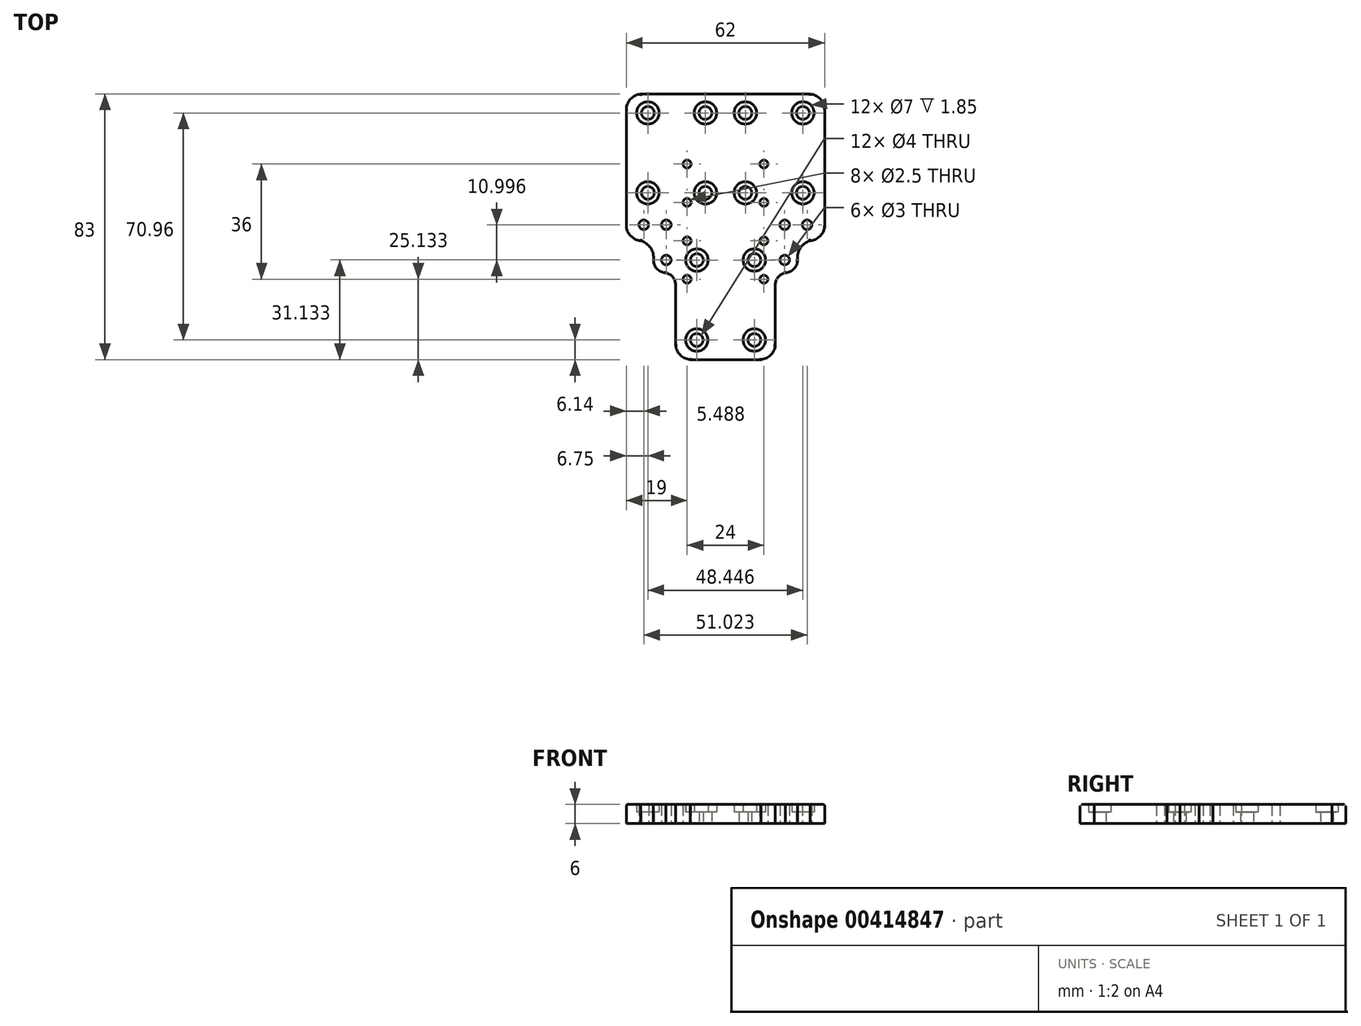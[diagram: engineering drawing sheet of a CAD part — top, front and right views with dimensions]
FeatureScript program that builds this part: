
annotation { "Feature Type Name" : "Feature", "Feature Type Description" : "" }
export const myFeature = defineFeature(function(context is Context, id is Id, definition is map)
    precondition{}
    {
        {
            var Q0;
            Q0=qCreatedBy(makeId("Top.planeOp"),FACE);
            cPlane(context, id + "F0", {"entities" : qUnion([Q0]), "cplaneType" : CPlaneType.OFFSET, "offset" : 15 * mm, "oppositeDirection" : true, "width" : 150 * mm, "height" : 150 * mm});
        }
        {
            var Q0;
            Q0=qCreatedBy(id+"F0.planeOp",FACE);
            var sketch = newSketch(context, id + "F1", { "sketchPlane" : qUnion([Q0])});
            skPoint(sketch, "E0.middle", {"position": v(0, 0) * mm});
            skLineSegment(sketch, "E1", {"start": v(-26.25, 37.6) * mm, "end": v(-22.25, 33.6) * mm, "construction": true});
            skLineSegment(sketch, "E2", {"start": v(-22.25, 37.6) * mm, "end": v(-26.25, 33.6) * mm, "construction": true});
            skLineSegment(sketch, "E3", {"start": v(-8.27, 37.6) * mm, "end": v(-4.27, 33.6) * mm, "construction": true});
            skLineSegment(sketch, "E4", {"start": v(-4.27, 37.6) * mm, "end": v(-8.27, 33.6) * mm, "construction": true});
            skLineSegment(sketch, "E5", {"start": v(4.21, 37.6) * mm, "end": v(8.21, 33.6) * mm, "construction": true});
            skLineSegment(sketch, "E6", {"start": v(8.21, 37.6) * mm, "end": v(4.21, 33.6) * mm, "construction": true});
            skLineSegment(sketch, "E7", {"start": v(22.2, 37.6) * mm, "end": v(26.2, 33.6) * mm, "construction": true});
            skLineSegment(sketch, "E8", {"start": v(26.2, 37.6) * mm, "end": v(22.2, 33.6) * mm, "construction": true});
            skLineSegment(sketch, "E9", {"start": v(-26.25, 12.63) * mm, "end": v(-22.25, 8.63) * mm, "construction": true});
            skLineSegment(sketch, "E10", {"start": v(-22.25, 12.63) * mm, "end": v(-26.25, 8.63) * mm, "construction": true});
            skLineSegment(sketch, "E11", {"start": v(-8.27, 12.63) * mm, "end": v(-4.27, 8.63) * mm, "construction": true});
            skLineSegment(sketch, "E12", {"start": v(-4.32, 12.68) * mm, "end": v(-8.32, 8.68) * mm, "construction": true});
            skLineSegment(sketch, "E13", {"start": v(4.21, 12.63) * mm, "end": v(8.21, 8.63) * mm, "construction": true});
            skLineSegment(sketch, "E14", {"start": v(8.22, 12.63) * mm, "end": v(4.21, 8.63) * mm, "construction": true});
            skLineSegment(sketch, "E15", {"start": v(22.2, 12.63) * mm, "end": v(26.2, 8.63) * mm, "construction": true});
            skLineSegment(sketch, "E16", {"start": v(26.2, 12.63) * mm, "end": v(22.2, 8.63) * mm, "construction": true});
            skLineSegment(sketch, "E17", {"start": v(-10.97, -8.37) * mm, "end": v(-6.88, -12.39) * mm, "construction": true});
            skLineSegment(sketch, "E18", {"start": v(-6.97, -8.37) * mm, "end": v(-10.97, -12.37) * mm, "construction": true});
            skLineSegment(sketch, "E19", {"start": v(7.01, -8.37) * mm, "end": v(11.01, -12.37) * mm, "construction": true});
            skLineSegment(sketch, "E20", {"start": v(11.01, -8.37) * mm, "end": v(7.01, -12.37) * mm, "construction": true});
            skLineSegment(sketch, "E21", {"start": v(-10.97, -33.36) * mm, "end": v(-6.97, -37.36) * mm, "construction": true});
            skLineSegment(sketch, "E22", {"start": v(-10.97, -37.36) * mm, "end": v(-6.97, -33.36) * mm, "construction": true});
            skLineSegment(sketch, "E23", {"start": v(7.01, -33.36) * mm, "end": v(11.01, -37.36) * mm, "construction": true});
            skLineSegment(sketch, "E24", {"start": v(7.01, -37.36) * mm, "end": v(11.01, -33.36) * mm, "construction": true});
            skCircle(sketch, "E25", {"center": v(-24.25, 35.6) * mm, "radius": 2 * mm});
            skCircle(sketch, "E26", {"center": v(-6.27, 35.6) * mm, "radius": 2 * mm});
            skCircle(sketch, "E27", {"center": v(6.21, 35.6) * mm, "radius": 2 * mm});
            skCircle(sketch, "E28", {"center": v(24.2, 35.6) * mm, "radius": 2 * mm});
            skCircle(sketch, "E29", {"center": v(24.2, 10.63) * mm, "radius": 2 * mm});
            skCircle(sketch, "E30", {"center": v(6.22, 10.63) * mm, "radius": 2 * mm});
            skCircle(sketch, "E31", {"center": v(-6.27, 10.63) * mm, "radius": 2 * mm});
            skCircle(sketch, "E32", {"center": v(-24.25, 10.63) * mm, "radius": 2 * mm});
            skCircle(sketch, "E33", {"center": v(-8.93, -10.38) * mm, "radius": 2 * mm});
            skCircle(sketch, "E34", {"center": v(9.01, -10.37) * mm, "radius": 2 * mm});
            skCircle(sketch, "E35", {"center": v(-8.97, -35.36) * mm, "radius": 2 * mm});
            skCircle(sketch, "E36", {"center": v(9.01, -35.36) * mm, "radius": 2 * mm});
            skCircle(sketch, "E37", {"center": v(-24.25, 35.6) * mm, "radius": 3.5 * mm});
            skCircle(sketch, "E38", {"center": v(-6.27, 35.6) * mm, "radius": 3.5 * mm});
            skCircle(sketch, "E39", {"center": v(6.21, 35.6) * mm, "radius": 3.5 * mm});
            skCircle(sketch, "E40", {"center": v(24.2, 35.6) * mm, "radius": 3.5 * mm});
            skCircle(sketch, "E41", {"center": v(-24.25, 10.63) * mm, "radius": 3.5 * mm});
            skCircle(sketch, "E42", {"center": v(-6.27, 10.63) * mm, "radius": 3.5 * mm});
            skCircle(sketch, "E43", {"center": v(6.22, 10.63) * mm, "radius": 3.5 * mm});
            skCircle(sketch, "E44", {"center": v(24.2, 10.63) * mm, "radius": 3.5 * mm});
            skCircle(sketch, "E45", {"center": v(-8.93, -10.38) * mm, "radius": 3.5 * mm});
            skCircle(sketch, "E46", {"center": v(9.01, -10.37) * mm, "radius": 3.5 * mm});
            skCircle(sketch, "E47", {"center": v(-8.97, -35.36) * mm, "radius": 3.5 * mm});
            skCircle(sketch, "E48", {"center": v(9.01, -35.36) * mm, "radius": 3.5 * mm});
            skLineSegment(sketch, "E49", {"start": v(0, 47.58) * mm, "end": v(0, -48.72) * mm, "construction": true});
            skLineSegment(sketch, "E50", {"start": v(-27.01, 2.13) * mm, "end": v(-24.01, -0.87) * mm});
            skLineSegment(sketch, "E51", {"start": v(-24.01, 2.13) * mm, "end": v(-27.01, -0.87) * mm, "construction": true});
            skLineSegment(sketch, "E52", {"start": v(-20, 2.13) * mm, "end": v(-17, -0.87) * mm, "construction": true});
            skLineSegment(sketch, "E53", {"start": v(-17, 2.13) * mm, "end": v(-20, -0.87) * mm, "construction": true});
            skLineSegment(sketch, "E54", {"start": v(17, 2.13) * mm, "end": v(20, -0.87) * mm, "construction": true});
            skLineSegment(sketch, "E55", {"start": v(20, 2.13) * mm, "end": v(17, -0.87) * mm, "construction": true});
            skLineSegment(sketch, "E56", {"start": v(24.01, 2.13) * mm, "end": v(27.01, -0.87) * mm, "construction": true});
            skLineSegment(sketch, "E57", {"start": v(27.01, 2.13) * mm, "end": v(24.01, -0.87) * mm, "construction": true});
            skLineSegment(sketch, "E58", {"start": v(17, -8.87) * mm, "end": v(20, -11.87) * mm, "construction": true});
            skLineSegment(sketch, "E59", {"start": v(20, -8.87) * mm, "end": v(17, -11.87) * mm, "construction": true});
            skLineSegment(sketch, "E60", {"start": v(-20, -8.87) * mm, "end": v(-17, -11.87) * mm, "construction": true});
            skLineSegment(sketch, "E61", {"start": v(-20, -11.87) * mm, "end": v(-17, -8.87) * mm, "construction": true});
            skCircle(sketch, "E62", {"center": v(25.51, 0.63) * mm, "radius": 1.5 * mm});
            skCircle(sketch, "E63", {"center": v(18.5, 0.63) * mm, "radius": 1.5 * mm});
            skCircle(sketch, "E64", {"center": v(18.5, -10.37) * mm, "radius": 1.5 * mm});
            skCircle(sketch, "E65", {"center": v(-18.5, 0.63) * mm, "radius": 1.5 * mm});
            skCircle(sketch, "E66", {"center": v(-25.51, 0.63) * mm, "radius": 1.5 * mm});
            skCircle(sketch, "E67", {"center": v(-18.5, -10.37) * mm, "radius": 1.5 * mm});
            skArc(sketch, "E68", {"start": v(-26.44, 41.5) * mm, "mid": v(-29.48, 40.1) * mm, "end": v(-31, 37.14) * mm});
            skArc(sketch, "E69.MirrorCS", {"start": v(26.44, 41.5) * mm, "mid": v(29.48, 40.1) * mm, "end": v(31, 37.14) * mm});
            skLineSegment(sketch, "E70", {"start": v(-34.26, 0) * mm, "end": v(34.55, 0) * mm, "construction": true});
            skLineSegment(sketch, "E71", {"start": v(26.44, 41.5) * mm, "end": v(-26.44, 41.5) * mm});
            skLineSegment(sketch, "E72.left", {"start": v(12, -16.37) * mm, "end": v(12, -4.37) * mm, "construction": true});
            skLineSegment(sketch, "E72.right", {"start": v(-12, -16.37) * mm, "end": v(-12, -4.37) * mm, "construction": true});
            skCircle(sketch, "E73", {"center": v(0, 0) * mm, "radius": 1 * mm, "construction": true});
            skLineSegment(sketch, "E74", {"start": v(-12, -16.37) * mm, "end": v(12, -16.37) * mm, "construction": true});
            skLineSegment(sketch, "E75", {"start": v(-12, -4.37) * mm, "end": v(12, -4.37) * mm, "construction": true});
            skCircle(sketch, "E76", {"center": v(12, -4.37) * mm, "radius": 1.25 * mm});
            skCircle(sketch, "E77.MirrorC", {"center": v(-12, -4.37) * mm, "radius": 1.25 * mm});
            skCircle(sketch, "E78.MirrorC", {"center": v(12, -16.37) * mm, "radius": 1.25 * mm});
            skCircle(sketch, "E79.MirrorC", {"center": v(-12, -16.37) * mm, "radius": 1.25 * mm});
            skLineSegment(sketch, "E80.left", {"start": v(12, -4.37) * mm, "end": v(12, 7.63) * mm, "construction": true});
            skLineSegment(sketch, "E80.right", {"start": v(-12, -4.37) * mm, "end": v(-12, 7.63) * mm, "construction": true});
            skLineSegment(sketch, "E81", {"start": v(-12, 7.63) * mm, "end": v(12, 7.63) * mm, "construction": true});
            skCircle(sketch, "E82", {"center": v(12, 7.63) * mm, "radius": 1.25 * mm});
            skCircle(sketch, "E83.MirrorC", {"center": v(-12, 7.63) * mm, "radius": 1.25 * mm});
            skLineSegment(sketch, "E84.left", {"start": v(12, 7.63) * mm, "end": v(12, 19.63) * mm, "construction": true});
            skLineSegment(sketch, "E84.right", {"start": v(-12, 7.63) * mm, "end": v(-12, 19.63) * mm, "construction": true});
            skLineSegment(sketch, "E85", {"start": v(-12, 19.63) * mm, "end": v(12, 19.63) * mm, "construction": true});
            skCircle(sketch, "E86", {"center": v(12, 19.63) * mm, "radius": 1.25 * mm});
            skCircle(sketch, "E87.MirrorC", {"center": v(-12, 19.63) * mm, "radius": 1.25 * mm});
            skArc(sketch, "E88.MirrorCS", {"start": v(26.44, -4.36) * mm, "mid": v(29.48, -2.97) * mm, "end": v(31, 0) * mm});
            skLineSegment(sketch, "E89", {"start": v(31, 37.14) * mm, "end": v(31, 0) * mm});
            skArc(sketch, "E90.MirrorCS", {"start": v(-26.44, -4.36) * mm, "mid": v(-29.48, -2.97) * mm, "end": v(-31, 0) * mm});
            skLineSegment(sketch, "E91", {"start": v(-31, 37.14) * mm, "end": v(-31, 0) * mm});
            skArc(sketch, "E92.MirrorCS", {"start": v(-11.03, -41.5) * mm, "mid": v(-14.07, -40.1) * mm, "end": v(-15.59, -37.14) * mm});
            skArc(sketch, "E93", {"start": v(-22.51, -10.35) * mm, "mid": v(-23.37, -6.63) * mm, "end": v(-26.44, -4.36) * mm});
            skLineSegment(sketch, "E94", {"start": v(-15.59, -37.14) * mm, "end": v(-15.59, -18.13) * mm});
            skArc(sketch, "E95", {"start": v(-15.59, -18.13) * mm, "mid": v(-16.45, -15.7) * mm, "end": v(-18.66, -14.37) * mm});
            skArc(sketch, "E96", {"start": v(-22.51, -10.35) * mm, "mid": v(-21.4, -13.14) * mm, "end": v(-18.66, -14.37) * mm});
            skArc(sketch, "E97.MirrorCS", {"start": v(22.51, -10.35) * mm, "mid": v(23.37, -6.63) * mm, "end": v(26.44, -4.36) * mm});
            skArc(sketch, "E98.MirrorCS", {"start": v(22.51, -10.35) * mm, "mid": v(21.4, -13.14) * mm, "end": v(18.66, -14.37) * mm});
            skArc(sketch, "E99.MirrorCS", {"start": v(15.59, -18.13) * mm, "mid": v(16.45, -15.7) * mm, "end": v(18.66, -14.37) * mm});
            skLineSegment(sketch, "E100.MirrorCS", {"start": v(15.59, -37.14) * mm, "end": v(15.59, -18.13) * mm});
            skArc(sketch, "E101.MirrorCS", {"start": v(11.03, -41.5) * mm, "mid": v(14.07, -40.1) * mm, "end": v(15.59, -37.14) * mm});
            skLineSegment(sketch, "E102", {"start": v(-11.03, -41.5) * mm, "end": v(11.03, -41.5) * mm});
            skSolve(sketch);
        }
        {
            var Q0;
            Q0=makeQuery(id+"F1.imprint","IMPRINT",FACE,{"disambiguationData":[TD([[makeQuery(id+"F1.imprint","IMPRINT",EDGE,{"derivedFrom":sQuery(id+"F1.wireOp",EDGE,"E37")}),-1.0]])]});
            var Q1;
            {var subQ12=sQuery(id+"F1.wireOp",EDGE,"pzuTnQxO-lV87-fYSm-Gx9G-mAiwIQIc8dDl");Q1=makeQuery(id+"F1.imprint","IMPRINT",FACE,{"disambiguationData":[TD([[makeQuery(id+"F1.imprint","IMPRINT",EDGE,{"derivedFrom":subQ12}),-1.0]])]});}
            var Q2;
            {var subQ1=sQuery(id+"F1.wireOp",EDGE,"pzuTnQxO-lV87-fYSm-Gx9G-mAiwIQIc8dDl");Q2=makeQuery(id+"F1.imprint","IMPRINT",FACE,{"disambiguationData":[TD([[makeQuery(id+"F1.imprint","IMPRINT",EDGE,{"derivedFrom":subQ1}),1.0]])]});}
            var Q3;
            {var subQ12=sQuery(id+"F1.wireOp",EDGE,"efa04ed1-a487-4949-b661-946b3568b5050.MirrorCS");Q3=makeQuery(id+"F1.imprint","IMPRINT",FACE,{"disambiguationData":[TD([[makeQuery(id+"F1.imprint","IMPRINT",EDGE,{"derivedFrom":subQ12}),1.0]])]});}
            var Q4;
            {var subQ4=sQuery(id+"F1.wireOp",EDGE,"E72.left");Q4=makeQuery(id+"F1.imprint","IMPRINT",FACE,{"disambiguationData":[TD([[makeQuery(id+"F1.imprint","IMPRINT",EDGE,{"derivedFrom":subQ4}),1.0]])]});}
            var Q5;
            {var subQ1=sQuery(id+"F1.wireOp",EDGE,"jk487AJZ-i1Am-lmEW-zcT6-8KVyPQAgBlb1.bottom");Q5=makeQuery(id+"F1.imprint","IMPRINT",FACE,{"disambiguationData":[TD([[makeQuery(id+"F1.imprint","IMPRINT",EDGE,{"derivedFrom":subQ1}),-1.0]])]});}
            var Q6;
            {var subQ4=sQuery(id+"F1.wireOp",EDGE,"E72.right");Q6=makeQuery(id+"F1.imprint","IMPRINT",FACE,{"disambiguationData":[TD([[makeQuery(id+"F1.imprint","IMPRINT",EDGE,{"derivedFrom":subQ4}),-1.0]])]});}
            var Q7;
            {var subQ1=sQuery(id+"F1.wireOp",EDGE,"jk487AJZ-i1Am-lmEW-zcT6-8KVyPQAgBlb1.left");var subQ3=sQuery(id+"F1.wireOp",EDGE,"8fUSbGhS-PyZG-xoJf-GsF2-3zE0cOOII221");var subQ4=makeQuery(id+"F1.imprint","INTERSECT",VERTEX,{"derivedFrom":[subQ1,subQ3]});Q7=makeQuery(id+"F1.imprint","IMPRINT",FACE,{"disambiguationData":[TD([[makeQuery(id+"F1.imprint","IMPRINT",EDGE,{"disambiguationData":[TD([[subQ4,-1.0]])],"derivedFrom":subQ3}),-1.0]])]});}
            var Q8;
            {var subQ0=sQuery(id+"F1.wireOp",EDGE,"FejcTz6K-61PN-e2Y3-l5dI-ztipBC45bLu5.bottom");var subQ1=sQuery(id+"F1.wireOp",EDGE,"jk487AJZ-i1Am-lmEW-zcT6-8KVyPQAgBlb1.right");var subQ2=makeQuery(id+"F1.imprint","INTERSECT",VERTEX,{"derivedFrom":[subQ1,subQ0]});Q8=makeQuery(id+"F1.imprint","IMPRINT",FACE,{"disambiguationData":[TD([[makeQuery(id+"F1.imprint","IMPRINT",EDGE,{"disambiguationData":[TD([[subQ2,1.0]])],"derivedFrom":subQ1}),-1.0]])]});}
            var Q9;
            {var subQ0=sQuery(id+"F1.wireOp",EDGE,"e855c95f-44d0-4618-945e-e5d8c2a51f020.MirrorCS");var subQ3=sQuery(id+"F1.wireOp",EDGE,"FejcTz6K-61PN-e2Y3-l5dI-ztipBC45bLu5.right");var subQ5=makeQuery(id+"F1.imprint","INTERSECT",VERTEX,{"derivedFrom":[subQ3,subQ0]});Q9=makeQuery(id+"F1.imprint","IMPRINT",FACE,{"disambiguationData":[TD([[makeQuery(id+"F1.imprint","IMPRINT",EDGE,{"disambiguationData":[TD([[subQ5,1.0]])],"derivedFrom":subQ3}),1.0]])]});}
            extrude(context, id + "F2", {"entities" : qUnion([Q0, Q1, Q2, Q3, Q4, Q5, Q6, Q7, Q8, Q9]), "depth" : 6 * mm});
        }
        {
            var Q0;
            Q0=makeQuery(id+"F1.imprint","IMPRINT",FACE,{"disambiguationData":[TD([[makeQuery(id+"F1.imprint","IMPRINT",EDGE,{"derivedFrom":sQuery(id+"F1.wireOp",EDGE,"E25")}),-1.0]])]});
            var Q1;
            Q1=makeQuery(id+"F1.imprint","IMPRINT",FACE,{"disambiguationData":[TD([[makeQuery(id+"F1.imprint","IMPRINT",EDGE,{"derivedFrom":sQuery(id+"F1.wireOp",EDGE,"E26")}),-1.0]])]});
            var Q2;
            Q2=makeQuery(id+"F1.imprint","IMPRINT",FACE,{"disambiguationData":[TD([[makeQuery(id+"F1.imprint","IMPRINT",EDGE,{"derivedFrom":sQuery(id+"F1.wireOp",EDGE,"E27")}),-1.0]])]});
            var Q3;
            Q3=makeQuery(id+"F1.imprint","IMPRINT",FACE,{"disambiguationData":[TD([[makeQuery(id+"F1.imprint","IMPRINT",EDGE,{"derivedFrom":sQuery(id+"F1.wireOp",EDGE,"E28")}),-1.0]])]});
            var Q4;
            Q4=makeQuery(id+"F1.imprint","IMPRINT",FACE,{"disambiguationData":[TD([[makeQuery(id+"F1.imprint","IMPRINT",EDGE,{"derivedFrom":sQuery(id+"F1.wireOp",EDGE,"E29")}),-1.0]])]});
            var Q5;
            Q5=makeQuery(id+"F1.imprint","IMPRINT",FACE,{"disambiguationData":[TD([[makeQuery(id+"F1.imprint","IMPRINT",EDGE,{"derivedFrom":sQuery(id+"F1.wireOp",EDGE,"E30")}),-1.0]])]});
            var Q6;
            Q6=makeQuery(id+"F1.imprint","IMPRINT",FACE,{"disambiguationData":[TD([[makeQuery(id+"F1.imprint","IMPRINT",EDGE,{"derivedFrom":sQuery(id+"F1.wireOp",EDGE,"E31")}),-1.0]])]});
            var Q7;
            Q7=makeQuery(id+"F1.imprint","IMPRINT",FACE,{"disambiguationData":[TD([[makeQuery(id+"F1.imprint","IMPRINT",EDGE,{"derivedFrom":sQuery(id+"F1.wireOp",EDGE,"E32")}),-1.0]])]});
            var Q8;
            Q8=makeQuery(id+"F1.imprint","IMPRINT",FACE,{"disambiguationData":[TD([[makeQuery(id+"F1.imprint","IMPRINT",EDGE,{"derivedFrom":sQuery(id+"F1.wireOp",EDGE,"E33")}),-1.0]])]});
            var Q9;
            Q9=makeQuery(id+"F1.imprint","IMPRINT",FACE,{"disambiguationData":[TD([[makeQuery(id+"F1.imprint","IMPRINT",EDGE,{"derivedFrom":sQuery(id+"F1.wireOp",EDGE,"E34")}),-1.0]])]});
            var Q10;
            Q10=makeQuery(id+"F1.imprint","IMPRINT",FACE,{"disambiguationData":[TD([[makeQuery(id+"F1.imprint","IMPRINT",EDGE,{"derivedFrom":sQuery(id+"F1.wireOp",EDGE,"E36")}),-1.0]])]});
            var Q11;
            Q11=makeQuery(id+"F1.imprint","IMPRINT",FACE,{"disambiguationData":[TD([[makeQuery(id+"F1.imprint","IMPRINT",EDGE,{"derivedFrom":sQuery(id+"F1.wireOp",EDGE,"E35")}),-1.0]])]});
            extrude(context, id + "F3", {"entities" : qUnion([Q0, Q1, Q2, Q3, Q4, Q5, Q6, Q7, Q8, Q9, Q10, Q11]), "operationType" : NewBodyOperationType.ADD, "depth" : 3.65 * mm});
        }
        {
            var Q0;
            Q0=makeQuery(id+"F2.opExtrude","CAP_FACE",FACE,{"disambiguationData":[OSD([sQuery(id+"F1.wireOp",EDGE,"E37"),sQuery(id+"F1.wireOp",EDGE,"E38"),sQuery(id+"F1.wireOp",EDGE,"E39"),sQuery(id+"F1.wireOp",EDGE,"E40"),sQuery(id+"F1.wireOp",EDGE,"E41"),sQuery(id+"F1.wireOp",EDGE,"E42"),sQuery(id+"F1.wireOp",EDGE,"E43"),sQuery(id+"F1.wireOp",EDGE,"E44"),sQuery(id+"F1.wireOp",EDGE,"E45"),sQuery(id+"F1.wireOp",EDGE,"E46"),sQuery(id+"F1.wireOp",EDGE,"E47"),sQuery(id+"F1.wireOp",EDGE,"E48"),sQuery(id+"F1.wireOp",EDGE,"E62"),sQuery(id+"F1.wireOp",EDGE,"E63"),sQuery(id+"F1.wireOp",EDGE,"E64"),sQuery(id+"F1.wireOp",EDGE,"E65"),sQuery(id+"F1.wireOp",EDGE,"E66"),sQuery(id+"F1.wireOp",EDGE,"E67"),sQuery(id+"F1.wireOp",EDGE,"E68"),sQuery(id+"F1.wireOp",EDGE,"E69.MirrorCS"),sQuery(id+"F1.wireOp",EDGE,"E71"),sQuery(id+"F1.wireOp",EDGE,"E76"),sQuery(id+"F1.wireOp",EDGE,"E77.MirrorC"),sQuery(id+"F1.wireOp",EDGE,"E78.MirrorC"),sQuery(id+"F1.wireOp",EDGE,"E79.MirrorC"),sQuery(id+"F1.wireOp",EDGE,"E82"),sQuery(id+"F1.wireOp",EDGE,"E83.MirrorC"),sQuery(id+"F1.wireOp",EDGE,"E86"),sQuery(id+"F1.wireOp",EDGE,"E87.MirrorC"),sQuery(id+"F1.wireOp",EDGE,"E88.MirrorCS"),sQuery(id+"F1.wireOp",EDGE,"E89"),sQuery(id+"F1.wireOp",EDGE,"E90.MirrorCS"),sQuery(id+"F1.wireOp",EDGE,"E91"),sQuery(id+"F1.wireOp",EDGE,"E92.MirrorCS"),sQuery(id+"F1.wireOp",EDGE,"E93"),sQuery(id+"F1.wireOp",EDGE,"E94"),sQuery(id+"F1.wireOp",EDGE,"E95"),sQuery(id+"F1.wireOp",EDGE,"E96"),sQuery(id+"F1.wireOp",EDGE,"E97.MirrorCS"),sQuery(id+"F1.wireOp",EDGE,"E98.MirrorCS"),sQuery(id+"F1.wireOp",EDGE,"E99.MirrorCS"),sQuery(id+"F1.wireOp",EDGE,"E100.MirrorCS"),sQuery(id+"F1.wireOp",EDGE,"E101.MirrorCS"),sQuery(id+"F1.wireOp",EDGE,"E102")])],"isStart":false});
            fillet(context, id + "F4", {"entities" : qUnion([Q0]), "radius" : 0.5 * mm, "tangentPropagation" : true, "allowEdgeOverflow" : false});
        }
    });
